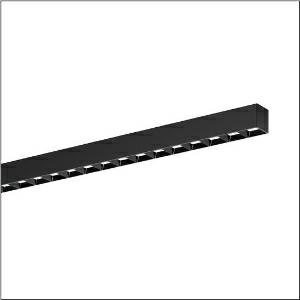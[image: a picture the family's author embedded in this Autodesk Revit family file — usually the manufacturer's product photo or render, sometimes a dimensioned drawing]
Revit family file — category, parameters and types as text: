
# Revit family: silica_21_51mx21dc3abb
name_source: partatom
category: Lighting Fixtures
units: mm (PartAtom-declared; Revit-internal decimal feet)

## family parameters
Cut with Voids When Loaded = No
Host = Face
Light Source = No
Part Type = Normal
Room Calculation Point = No
Round Connector Dimension = Use Diameter
Shared = No

## types (1)
- --- (1 x LED, 10800 lm, 69.3 W, 3000K)
    Apparent Load = 69 VA
    CIE Flux Codes = 87 99 100 100 100
    Color Rendering = 80
    Color Temperature = 3000K
    Default Elevation = 1800 mm
    Description = Silica 21, office luminaire, primary light control with darklight reflector, of PMMA, black, CAT 2 (L<= 3000cd/m²), light emission: direct distribution, primary light characteristic: symmetric, installation type: surface-mounted, LED, rated luminous flux: 10.800lm, luminous efficacy: 156lm/W, light colour: 830, colour temperature: 3000K, control gear: DALI 2, with terminal, 3+2-pole, max. 2.5mm², mains connection: 220..240V, AC, 50/60Hz, luminaire housing, of aluminium, matt jet black (RAL 9005), length: 3.004mm, width: 53mm, height: 53mm, protection rating (complete): IP20, insulation class (complete): insulation class I (protective earthing), certification: CE, permissible operating ambient temperature: 0..+35°C, standard: EN 50419, packaging unit: 1 piece
    Height = 53 mm
    Lamp = 1 x LED
    Lamp Light Flux = 10800 lm
    Lamp Power = 69.3 W
    Lamp count = 1
    Length = 3004 mm
    Luminous efficacy = 156 lm/W
    Manufacturer = Siteco
    ModVariant = No
    Model = 51MX21DC3ABB
    Mounting Place = Ceiling
    Mounting Type = Surface mounted
    Number of Poles = 1
    OnlyDefault = Yes
    Power Factor = 1
    Product Name = Silica 21
    Product group = office luminaire | ceiling mounted
    ProductGroupID = 301
    Protection Class = Protection class I
    Protection Degree = IP 20
    RLX_Detail_Level = 1
    RLX_Emergency_Light_Flux = 0 lm
    RLX_Emergency_Type = 0
    RLX_Emergency_Type_DB = No
    RlxData = <blob elided: 63881 chars, md5=14cf4c8a>
    Socket = socket
    Standby Power = 0 W
    System Light Flux = 10800 lm
    System Power = 69 W
    Type Comments = factory setting: luminous flux: 100 % | dim-lin: 254 | 393 mA
    Type Image = l_1335908.jpg
    URL = http://relux.com
    VarID = @adj_123831
    Voltage = 0 V
    Weight = 0.00 kg
    Width = 53 mm

## geometry (parser evidence)
native form markers: Blend x4, Sweep x10
no freeform markers — native parametric forms only
